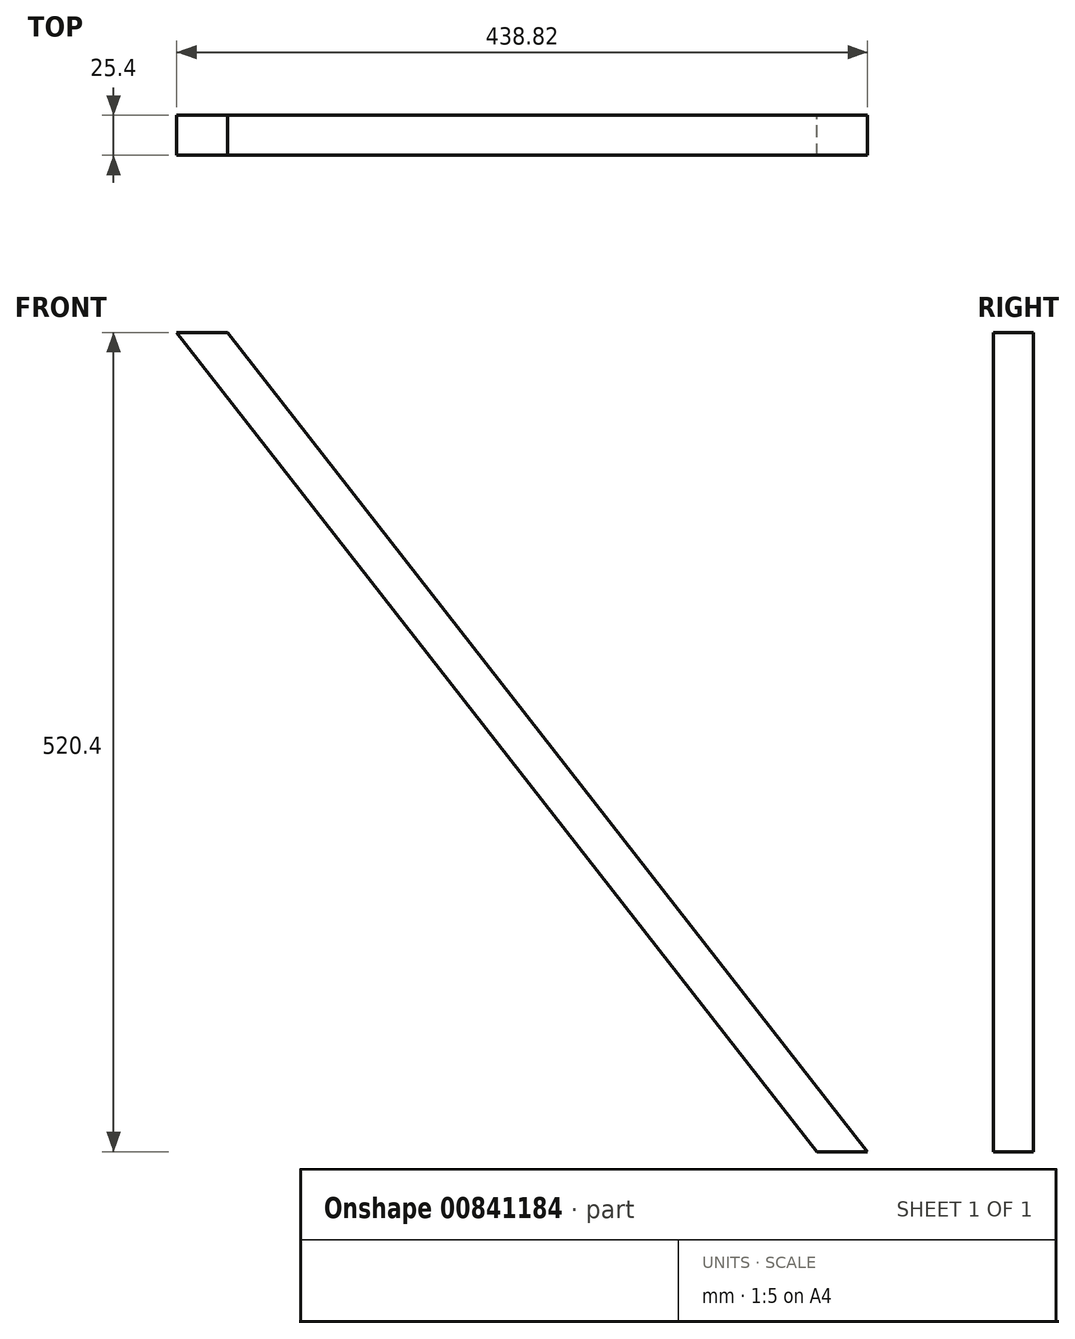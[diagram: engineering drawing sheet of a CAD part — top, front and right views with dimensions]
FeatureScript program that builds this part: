
annotation { "Feature Type Name" : "Feature", "Feature Type Description" : "" }
export const myFeature = defineFeature(function(context is Context, id is Id, definition is map)
    precondition{}
    {
        {
            var Q0;
            Q0=qCreatedBy(makeId("Front.planeOp"),FACE);
            var sketch = newSketch(context, id + "F0", { "sketchPlane" : qUnion([Q0])});
            skLineSegment(sketch, "E0", {"start": v(0, 0) * mm, "end": v(406.58, -520.4) * mm});
            skLineSegment(sketch, "E1", {"start": v(438.82, -520.4) * mm, "end": v(32.23, 0) * mm});
            skLineSegment(sketch, "E2", {"start": v(32.23, 0) * mm, "end": v(0, 0) * mm});
            skLineSegment(sketch, "E3", {"start": v(0, 0) * mm, "end": v(210.26, 0) * mm, "construction": true});
            skLineSegment(sketch, "E4", {"start": v(438.82, -520.4) * mm, "end": v(406.58, -520.4) * mm});
            skSolve(sketch);
        }
        {
            var Q0;
            Q0 = qSketchRegion(id + "F0", true);
            extrude(context, id + "F1", {"entities" : qUnion([Q0]), "depth" : 25.4 * mm, "offsetDistance" : 25.4 * mm});
        }
    });
